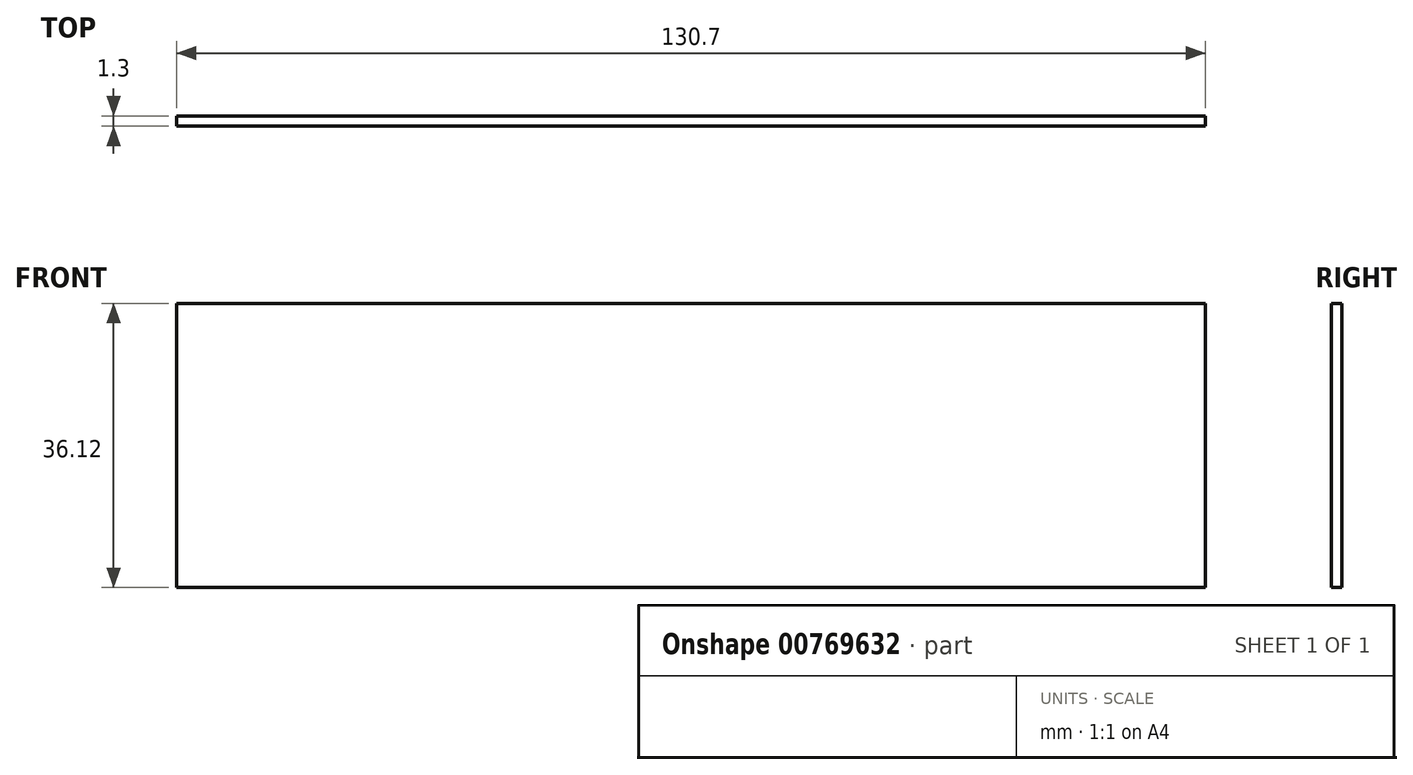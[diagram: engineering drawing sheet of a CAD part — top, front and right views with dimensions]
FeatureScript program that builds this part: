
annotation { "Feature Type Name" : "Feature", "Feature Type Description" : "" }
export const myFeature = defineFeature(function(context is Context, id is Id, definition is map)
    precondition{}
    {
        {
            var Q0;
            Q0=qCreatedBy(makeId("Front.planeOp"),FACE);
            var sketch = newSketch(context, id + "F0", { "sketchPlane" : qUnion([Q0])});
            skLineSegment(sketch, "E0.bottom", {"start": v(-67.1, 59.03) * mm, "end": v(63.6, 59.03) * mm});
            skLineSegment(sketch, "E0.top", {"start": v(-67.1, 22.91) * mm, "end": v(63.6, 22.91) * mm});
            skLineSegment(sketch, "E0.left", {"start": v(-67.1, 59.03) * mm, "end": v(-67.1, 22.91) * mm});
            skLineSegment(sketch, "E0.right", {"start": v(63.6, 59.03) * mm, "end": v(63.6, 22.91) * mm});
            skSolve(sketch);
        }
        {
            var Q0;
            Q0 = qSketchRegion(id + "F0", true);
            var sketch = newSketch(context, id + "F1", { "sketchPlane" : qUnion([Q0])});
            skSolve(sketch);
        }
        {
            var Q0;
            Q0=makeQuery(id+"F0.imprint","IMPRINT",FACE,{"disambiguationData":[TD([[makeQuery(id+"F0.imprint","IMPRINT",EDGE,{"derivedFrom":sQuery(id+"F0.wireOp",EDGE,"E0.bottom")}),-1.0]])]});
            extrude(context, id + "F2", {"entities" : qUnion([Q0]), "oppositeDirection" : true, "depth" : 1.3 * mm, "offsetDistance" : 25.4 * mm});
        }
    });
